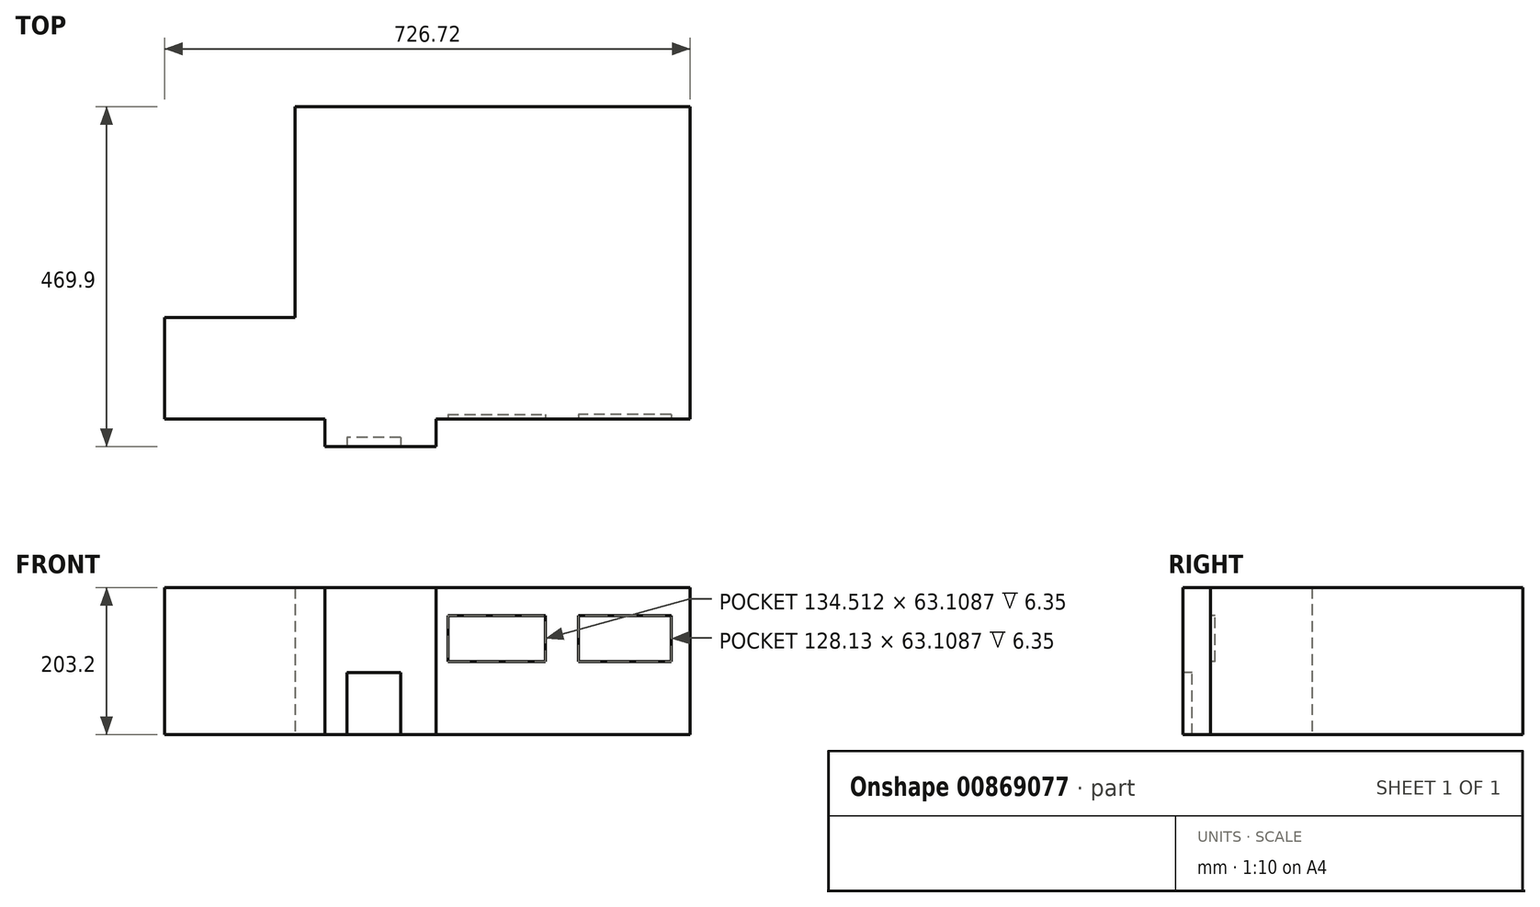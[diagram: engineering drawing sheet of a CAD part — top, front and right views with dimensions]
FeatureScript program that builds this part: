
annotation { "Feature Type Name" : "Feature", "Feature Type Description" : "" }
export const myFeature = defineFeature(function(context is Context, id is Id, definition is map)
    precondition{}
    {
        {
            var Q0;
            Q0=qCreatedBy(makeId("Top.planeOp"),FACE);
            var sketch = newSketch(context, id + "F0", { "sketchPlane" : qUnion([Q0])});
            skLineSegment(sketch, "E0", {"start": v(-345.72, 0) * mm, "end": v(-345.72, 291.4) * mm});
            skLineSegment(sketch, "E1", {"start": v(-345.72, 291.4) * mm, "end": v(200.38, 291.4) * mm});
            skLineSegment(sketch, "E2", {"start": v(200.38, 291.4) * mm, "end": v(200.38, -140.4) * mm});
            skLineSegment(sketch, "E3", {"start": v(200.38, -140.4) * mm, "end": v(-150.99, -140.4) * mm});
            skLineSegment(sketch, "E4", {"start": v(-150.99, -140.4) * mm, "end": v(-150.99, -178.5) * mm});
            skLineSegment(sketch, "E5", {"start": v(-150.99, -178.5) * mm, "end": v(-304.8, -178.5) * mm});
            skLineSegment(sketch, "E6", {"start": v(-304.8, -178.5) * mm, "end": v(-304.8, -140.4) * mm});
            skLineSegment(sketch, "E7", {"start": v(-304.8, -140.4) * mm, "end": v(-345.72, -140.4) * mm});
            skLineSegment(sketch, "E8", {"start": v(-345.72, -140.4) * mm, "end": v(-526.34, -140.4) * mm});
            skLineSegment(sketch, "E9", {"start": v(-526.34, -140.4) * mm, "end": v(-526.34, 0) * mm});
            skLineSegment(sketch, "E10", {"start": v(-526.34, 0) * mm, "end": v(-345.72, 0) * mm});
            skLineSegment(sketch, "E11", {"start": v(-345.72, 0) * mm, "end": v(-345.72, -140.4) * mm});
            skLineSegment(sketch, "E12", {"start": v(-345.72, 0) * mm, "end": v(-151.47, 0) * mm});
            skLineSegment(sketch, "E13", {"start": v(-151.47, 0) * mm, "end": v(-151.47, 195.74) * mm});
            skLineSegment(sketch, "E14", {"start": v(-151.47, 195.74) * mm, "end": v(-345.72, 195.74) * mm});
            skLineSegment(sketch, "E15", {"start": v(200.38, 0) * mm, "end": v(0, 0) * mm});
            skLineSegment(sketch, "E16", {"start": v(0, 0) * mm, "end": v(0, -140.4) * mm});
            skLineSegment(sketch, "E17", {"start": v(200.38, 178.37) * mm, "end": v(0, 178.37) * mm});
            skLineSegment(sketch, "E18", {"start": v(0, 178.37) * mm, "end": v(0, 291.4) * mm});
            skSolve(sketch);
        }
        {
            var Q0;
            Q0 = qSketchRegion(id + "F0", true);
            extrude(context, id + "F1", {"entities" : qUnion([Q0]), "depth" : 203.2 * mm, "offsetDistance" : 25.4 * mm});
        }
        {
            var Q0;
            Q0=makeQuery(id+"F1.opExtrude","SWEPT_FACE",FACE,{"disambiguationData":[OSD([sQuery(id+"F0.wireOp",EDGE,"E5")])]});
            var sketch = newSketch(context, id + "F2", { "sketchPlane" : qUnion([Q0])});
            skLineSegment(sketch, "E19", {"start": v(-274.27, 0) * mm, "end": v(-274.27, 85.82) * mm});
            skLineSegment(sketch, "E20", {"start": v(-274.27, 85.82) * mm, "end": v(-199.69, 85.82) * mm});
            skLineSegment(sketch, "E21", {"start": v(-199.69, 85.82) * mm, "end": v(-199.69, 0) * mm});
            skLineSegment(sketch, "E22", {"start": v(-274.27, 0) * mm, "end": v(-199.69, 0) * mm});
            skSolve(sketch);
        }
        {
            var Q0;
            Q0 = qSketchRegion(id + "F2", true);
            extrude(context, id + "F3", {"entities" : qUnion([Q0]), "operationType" : NewBodyOperationType.REMOVE, "oppositeDirection" : true, "depth" : 12.7 * mm, "offsetDistance" : 25.4 * mm});
        }
        {
            var Q0;
            Q0=makeQuery(id+"F1.opExtrude","SWEPT_FACE",FACE,{"disambiguationData":[OSD([sQuery(id+"F0.wireOp",EDGE,"E3")])]});
            var sketch = newSketch(context, id + "F4", { "sketchPlane" : qUnion([Q0])});
            skLineSegment(sketch, "E23", {"start": v(-134.51, 164.23) * mm, "end": v(0, 164.23) * mm});
            skLineSegment(sketch, "E24", {"start": v(0, 164.23) * mm, "end": v(0, 101.12) * mm});
            skLineSegment(sketch, "E25", {"start": v(0, 101.12) * mm, "end": v(-134.51, 101.12) * mm});
            skLineSegment(sketch, "E26", {"start": v(-134.51, 101.12) * mm, "end": v(-134.51, 164.23) * mm});
            skSolve(sketch);
        }
        {
            var Q0;
            Q0 = qSketchRegion(id + "F4", true);
            extrude(context, id + "F5", {"entities" : qUnion([Q0]), "operationType" : NewBodyOperationType.REMOVE, "oppositeDirection" : true, "depth" : 6.35 * mm, "offsetDistance" : 25.4 * mm});
        }
        {
            var Q0;
            Q0=makeQuery(id+"F1.opExtrude","SWEPT_FACE",FACE,{"disambiguationData":[OSD([sQuery(id+"F0.wireOp",EDGE,"E3")])]});
            var sketch = newSketch(context, id + "F6", { "sketchPlane" : qUnion([Q0])});
            skLineSegment(sketch, "E27", {"start": v(46.2, 164.23) * mm, "end": v(46.2, 101.12) * mm});
            skLineSegment(sketch, "E28", {"start": v(46.2, 101.12) * mm, "end": v(174.34, 101.12) * mm});
            skLineSegment(sketch, "E29", {"start": v(174.34, 101.12) * mm, "end": v(174.34, 164.23) * mm});
            skLineSegment(sketch, "E30", {"start": v(174.34, 164.23) * mm, "end": v(46.2, 164.23) * mm});
            skSolve(sketch);
        }
        {
            var Q0;
            Q0 = qSketchRegion(id + "F6", true);
            extrude(context, id + "F7", {"entities" : qUnion([Q0]), "operationType" : NewBodyOperationType.REMOVE, "oppositeDirection" : true, "depth" : 6.35 * mm, "offsetDistance" : 25.4 * mm});
        }
    });
